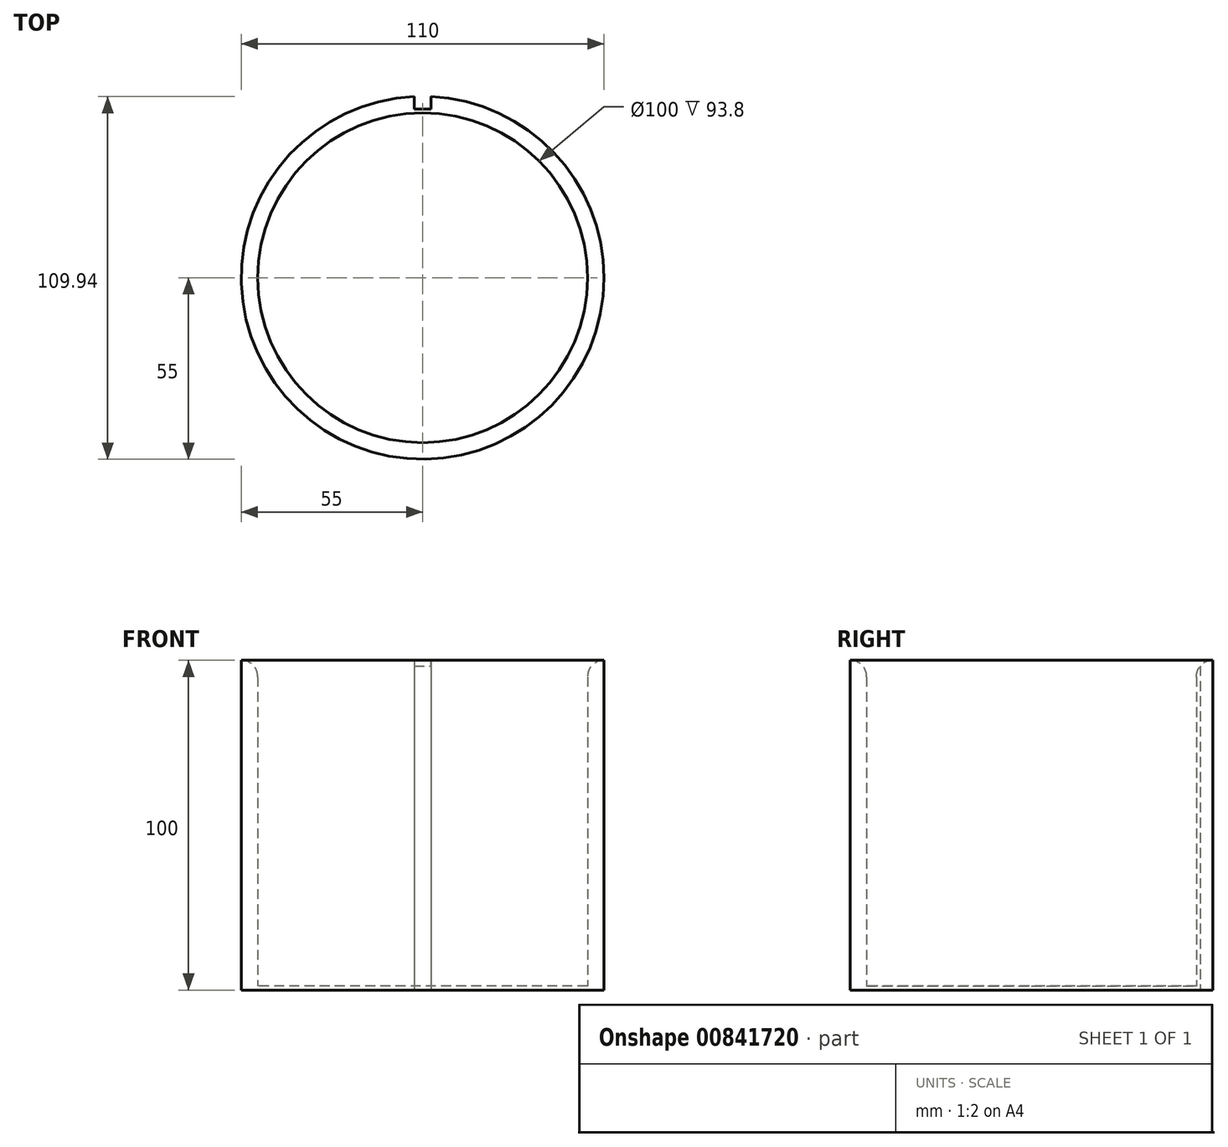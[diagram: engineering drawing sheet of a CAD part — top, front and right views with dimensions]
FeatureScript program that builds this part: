
annotation { "Feature Type Name" : "Feature", "Feature Type Description" : "" }
export const myFeature = defineFeature(function(context is Context, id is Id, definition is map)
    precondition{}
    {
        {
            var Q0;
            Q0=qCreatedBy(makeId("Top.planeOp"),FACE);
            var sketch = newSketch(context, id + "F0", { "sketchPlane" : qUnion([Q0])});
            skCircle(sketch, "E0", {"center": v(0, 0) * mm, "radius": 50 * mm});
            skCircle(sketch, "E1", {"center": v(0, 0) * mm, "radius": 55 * mm});
            skSolve(sketch);
        }
        {
            var Q0;
            Q0=makeQuery(id+"F0.imprint","IMPRINT",FACE,{"disambiguationData":[TD([[makeQuery(id+"F0.imprint","IMPRINT",EDGE,{"derivedFrom":sQuery(id+"F0.wireOp",EDGE,"E0")}),-1.0]])]});
            extrude(context, id + "F1", {"entities" : qUnion([Q0]), "depth" : 100 * mm, "offsetDistance" : 25 * mm});
        }
        {
            var Q0;
            Q0=qCreatedBy(makeId("Top.planeOp"),FACE);
            var sketch = newSketch(context, id + "F2", { "sketchPlane" : qUnion([Q0])});
            skCircle(sketch, "E2", {"center": v(0, 0) * mm, "radius": 50 * mm});
            skSolve(sketch);
        }
        {
            var Q0;
            Q0=makeQuery(id+"F2.imprint","IMPRINT",FACE,{"disambiguationData":[TD([[makeQuery(id+"F2.imprint","IMPRINT",EDGE,{"derivedFrom":sQuery(id+"F2.wireOp",EDGE,"E2")}),1.0]])]});
            extrude(context, id + "F3", {"entities" : qUnion([Q0]), "operationType" : NewBodyOperationType.ADD, "depth" : 1.2 * mm, "offsetDistance" : 25 * mm});
        }
        {
            var Q0;
            Q0=qCreatedBy(makeId("Top.planeOp"),FACE);
            var sketch = newSketch(context, id + "F4", { "sketchPlane" : qUnion([Q0])});
            skLineSegment(sketch, "E3.bottom", {"start": v(-2.5, 56.17) * mm, "end": v(2.5, 56.17) * mm});
            skLineSegment(sketch, "E3.top", {"start": v(-2.5, 51.17) * mm, "end": v(2.5, 51.17) * mm});
            skLineSegment(sketch, "E3.left", {"start": v(-2.5, 56.17) * mm, "end": v(-2.5, 51.17) * mm});
            skLineSegment(sketch, "E3.right", {"start": v(2.5, 56.17) * mm, "end": v(2.5, 51.17) * mm});
            skSolve(sketch);
        }
        {
            var Q0;
            Q0 = qSketchRegion(id + "F4", true);
            extrude(context, id + "F5", {"entities" : qUnion([Q0]), "operationType" : NewBodyOperationType.REMOVE, "depth" : 200.6 * mm, "offsetDistance" : 25 * mm});
        }
        {
            var Q0;
            Q0=qCreatedBy(makeId("Right.planeOp"),FACE);
            var sketch = newSketch(context, id + "F6", { "sketchPlane" : qUnion([Q0])});
            skLineSegment(sketch, "E4", {"start": v(0, 0) * mm, "end": v(0, 197.23) * mm, "construction": true});
            skSolve(sketch);
        }
        {
            var Q0;
            Q0=makeQuery(id+"F1.opExtrude","CAP_EDGE",EDGE,{"disambiguationData":[OSD([sQuery(id+"F0.wireOp",EDGE,"E0")])],"isStart":false});
            fillet(context, id + "F7", {"entities" : qUnion([Q0]), "radius" : 5 * mm, "tangentPropagation" : true, "allowEdgeOverflow" : false});
        }
    });
